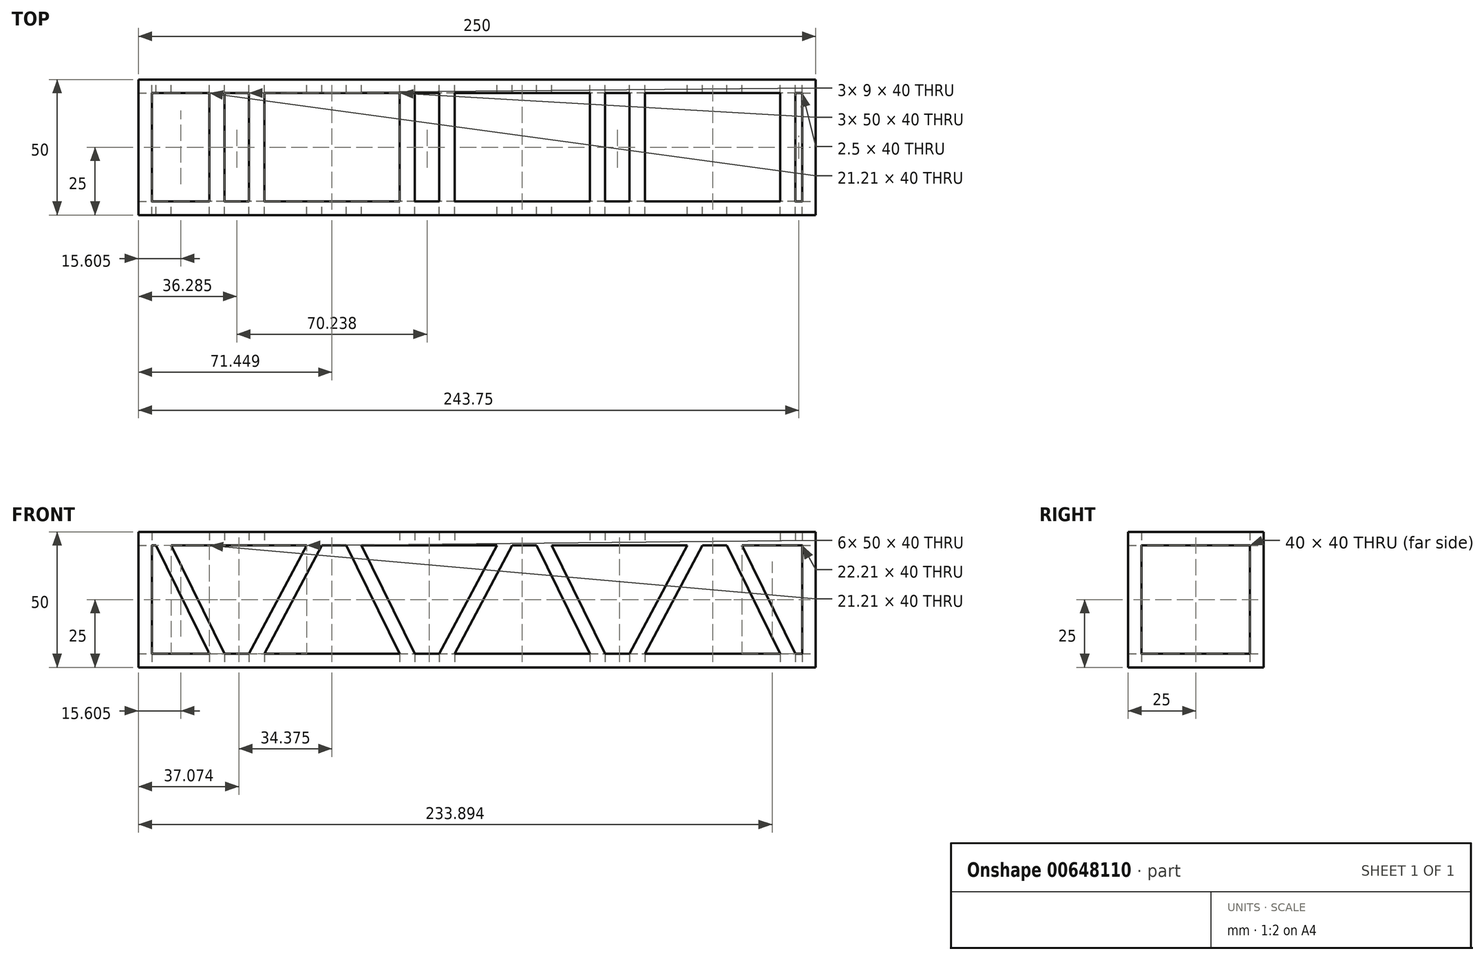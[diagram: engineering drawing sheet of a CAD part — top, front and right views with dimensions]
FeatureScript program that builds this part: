
annotation { "Feature Type Name" : "Feature", "Feature Type Description" : "" }
export const myFeature = defineFeature(function(context is Context, id is Id, definition is map)
    precondition{}
    {
        {
            var Q0;
            Q0=qCreatedBy(makeId("Front.planeOp"),FACE);
            var sketch = newSketch(context, id + "F0", { "sketchPlane" : qUnion([Q0])});
            skLineSegment(sketch, "E0", {"start": v(-152.14, 45) * mm, "end": v(97.86, 45) * mm});
            skLineSegment(sketch, "E1", {"start": v(97.86, 45) * mm, "end": v(97.86, -5) * mm});
            skLineSegment(sketch, "E2", {"start": v(97.86, -5) * mm, "end": v(-152.14, -5) * mm});
            skLineSegment(sketch, "E3", {"start": v(-152.14, -5) * mm, "end": v(-152.14, 45) * mm});
            skLineSegment(sketch, "E4", {"start": v(-145.64, 40) * mm, "end": v(-125.93, 0) * mm});
            skLineSegment(sketch, "E5", {"start": v(-111.35, 0) * mm, "end": v(-90.07, 40) * mm});
            skLineSegment(sketch, "E6", {"start": v(-69.83, 40) * mm, "end": v(-50.12, 0) * mm});
            skLineSegment(sketch, "E7", {"start": v(-41.12, 0) * mm, "end": v(-19.83, 40) * mm});
            skLineSegment(sketch, "E8", {"start": v(-5.16, 40) * mm, "end": v(14.55, 0) * mm});
            skLineSegment(sketch, "E9.0", {"start": v(84.79, 0) * mm, "end": v(34.79, 0) * mm});
            skLineSegment(sketch, "E10.0", {"start": v(-105.7, 0) * mm, "end": v(-84.4, 40) * mm});
            skLineSegment(sketch, "E11.0", {"start": v(0.41, 40) * mm, "end": v(20.12, 0) * mm});
            skLineSegment(sketch, "E12.0", {"start": v(34.79, 0) * mm, "end": v(56.07, 40) * mm});
            skLineSegment(sketch, "E13.trimOffspring", {"start": v(-140.07, 40) * mm, "end": v(-120.35, 0) * mm});
            skLineSegment(sketch, "E14.trimOffspring", {"start": v(-140.07, 40) * mm, "end": v(-90.07, 40) * mm});
            skLineSegment(sketch, "E15.trimOffspring", {"start": v(-75.4, 40) * mm, "end": v(-55.7, 0) * mm});
            skLineSegment(sketch, "E16.trimOffspring", {"start": v(-69.83, 40) * mm, "end": v(-19.83, 40) * mm});
            skLineSegment(sketch, "E17.trimOffspring", {"start": v(-84.4, 40) * mm, "end": v(-75.4, 40) * mm});
            skLineSegment(sketch, "E18.trimOffspring", {"start": v(-111.35, 0) * mm, "end": v(-120.35, 0) * mm});
            skLineSegment(sketch, "E19.trimOffspring", {"start": v(-125.93, 0) * mm, "end": v(-147.14, 0) * mm});
            skLineSegment(sketch, "E20.trimOffspring", {"start": v(-14.16, 40) * mm, "end": v(-5.16, 40) * mm});
            skLineSegment(sketch, "E21", {"start": v(0.41, 40) * mm, "end": v(50.41, 40) * mm});
            skLineSegment(sketch, "E22.trimOffspring", {"start": v(29.12, 0) * mm, "end": v(50.41, 40) * mm});
            skLineSegment(sketch, "E23.trimOffspring", {"start": v(-35.45, 0) * mm, "end": v(-14.16, 40) * mm});
            skLineSegment(sketch, "E24.trimOffspring", {"start": v(-55.7, 0) * mm, "end": v(-105.7, 0) * mm});
            skLineSegment(sketch, "E25.trimOffspring", {"start": v(-41.12, 0) * mm, "end": v(-50.12, 0) * mm});
            skLineSegment(sketch, "E26.trimOffspring", {"start": v(14.55, 0) * mm, "end": v(-35.45, 0) * mm});
            skLineSegment(sketch, "E27.trimOffspring", {"start": v(29.12, 0) * mm, "end": v(20.12, 0) * mm});
            skLineSegment(sketch, "E28", {"start": v(-147.14, 40) * mm, "end": v(-147.14, 0) * mm});
            skLineSegment(sketch, "E29", {"start": v(70.65, 40) * mm, "end": v(92.86, 40) * mm});
            skLineSegment(sketch, "E30", {"start": v(65.07, 40) * mm, "end": v(84.79, 0) * mm});
            skLineSegment(sketch, "E31", {"start": v(70.65, 40) * mm, "end": v(90.36, 0) * mm});
            skLineSegment(sketch, "E32", {"start": v(56.07, 40) * mm, "end": v(65.07, 40) * mm});
            skLineSegment(sketch, "E33", {"start": v(90.36, 0) * mm, "end": v(97.86, 0) * mm});
            skLineSegment(sketch, "E34", {"start": v(92.86, 0) * mm, "end": v(92.86, 40) * mm});
            skLineSegment(sketch, "E35", {"start": v(-147.14, 40) * mm, "end": v(-145.64, 40) * mm});
            skPoint(sketch, "E36.orphan", {"position": v(92.86, -5.07) * mm});
            skSolve(sketch);
        }
        {
            var Q0;
            {var subQ3=sQuery(id+"F0.wireOp",EDGE,"E0");Q0=makeQuery(id+"F0.imprint","IMPRINT",FACE,{"disambiguationData":[TD([[makeQuery(id+"F0.imprint","IMPRINT",EDGE,{"derivedFrom":subQ3}),-1.0]])]});}
            extrude(context, id + "F1", {"entities" : qUnion([Q0]), "depth" : 50 * mm, "offsetDistance" : 25 * mm});
        }
        {
            var Q0;
            Q0=makeQuery(id+"F1.opExtrude","SWEPT_FACE",FACE,{"disambiguationData":[OSD([sQuery(id+"F0.wireOp",EDGE,"E2")])]});
            var sketch = newSketch(context, id + "F2", { "sketchPlane" : qUnion([Q0])});
            skLineSegment(sketch, "E37.bottom", {"start": v(-147.14, 45) * mm, "end": v(-125.93, 45) * mm});
            skLineSegment(sketch, "E37.top", {"start": v(-147.14, 5) * mm, "end": v(-125.93, 5) * mm});
            skLineSegment(sketch, "E37.left", {"start": v(-147.14, 45) * mm, "end": v(-147.14, 5) * mm});
            skLineSegment(sketch, "E37.right", {"start": v(-125.93, 45) * mm, "end": v(-125.93, 5) * mm});
            skLineSegment(sketch, "E38.bottom", {"start": v(-120.35, 45) * mm, "end": v(-111.35, 45) * mm});
            skLineSegment(sketch, "E38.top", {"start": v(-120.35, 5) * mm, "end": v(-111.35, 5) * mm});
            skLineSegment(sketch, "E38.left", {"start": v(-120.35, 45) * mm, "end": v(-120.35, 5) * mm});
            skLineSegment(sketch, "E38.right", {"start": v(-111.35, 45) * mm, "end": v(-111.35, 5) * mm});
            skLineSegment(sketch, "E39.bottom", {"start": v(-105.7, 45) * mm, "end": v(-55.7, 45) * mm});
            skLineSegment(sketch, "E39.top", {"start": v(-105.7, 5) * mm, "end": v(-55.7, 5) * mm});
            skLineSegment(sketch, "E39.left", {"start": v(-105.7, 45) * mm, "end": v(-105.7, 5) * mm});
            skLineSegment(sketch, "E39.right", {"start": v(-55.7, 45) * mm, "end": v(-55.7, 5) * mm});
            skLineSegment(sketch, "E40.bottom", {"start": v(-50.12, 45) * mm, "end": v(-41.12, 45) * mm});
            skLineSegment(sketch, "E40.top", {"start": v(-50.12, 5) * mm, "end": v(-41.12, 5) * mm});
            skLineSegment(sketch, "E40.left", {"start": v(-50.12, 45) * mm, "end": v(-50.12, 5) * mm});
            skLineSegment(sketch, "E40.right", {"start": v(-41.12, 45) * mm, "end": v(-41.12, 5) * mm});
            skLineSegment(sketch, "E41.bottom", {"start": v(-35.45, 45) * mm, "end": v(14.55, 45) * mm});
            skLineSegment(sketch, "E41.top", {"start": v(-35.45, 5) * mm, "end": v(14.55, 5) * mm});
            skLineSegment(sketch, "E41.left", {"start": v(-35.45, 45) * mm, "end": v(-35.45, 5) * mm});
            skLineSegment(sketch, "E41.right", {"start": v(14.55, 45) * mm, "end": v(14.55, 5) * mm});
            skLineSegment(sketch, "E42.bottom", {"start": v(20.12, 45) * mm, "end": v(29.12, 45) * mm});
            skLineSegment(sketch, "E42.top", {"start": v(20.12, 5) * mm, "end": v(29.12, 5) * mm});
            skLineSegment(sketch, "E42.left", {"start": v(20.12, 45) * mm, "end": v(20.12, 5) * mm});
            skLineSegment(sketch, "E42.right", {"start": v(29.12, 45) * mm, "end": v(29.12, 5) * mm});
            skLineSegment(sketch, "E43.bottom", {"start": v(34.79, 45) * mm, "end": v(84.79, 45) * mm});
            skLineSegment(sketch, "E43.top", {"start": v(34.79, 5) * mm, "end": v(84.79, 5) * mm});
            skLineSegment(sketch, "E43.left", {"start": v(34.79, 45) * mm, "end": v(34.79, 5) * mm});
            skLineSegment(sketch, "E43.right", {"start": v(84.79, 45) * mm, "end": v(84.79, 5) * mm});
            skLineSegment(sketch, "E44.bottom", {"start": v(90.36, 45) * mm, "end": v(92.86, 45) * mm});
            skLineSegment(sketch, "E44.top", {"start": v(90.36, 5) * mm, "end": v(92.86, 5) * mm});
            skLineSegment(sketch, "E44.left", {"start": v(90.36, 45) * mm, "end": v(90.36, 5) * mm});
            skLineSegment(sketch, "E44.right", {"start": v(92.86, 45) * mm, "end": v(92.86, 5) * mm});
            skSolve(sketch);
        }
        {
            var Q0;
            Q0=makeQuery(id+"F2.imprint","IMPRINT",FACE,{"disambiguationData":[TD([[makeQuery(id+"F2.imprint","IMPRINT",EDGE,{"derivedFrom":sQuery(id+"F2.wireOp",EDGE,"E44.bottom")}),-1.0]])]});
            var Q1;
            Q1=makeQuery(id+"F2.imprint","IMPRINT",FACE,{"disambiguationData":[TD([[makeQuery(id+"F2.imprint","IMPRINT",EDGE,{"derivedFrom":sQuery(id+"F2.wireOp",EDGE,"E43.bottom")}),-1.0]])]});
            var Q2;
            Q2=makeQuery(id+"F2.imprint","IMPRINT",FACE,{"disambiguationData":[TD([[makeQuery(id+"F2.imprint","IMPRINT",EDGE,{"derivedFrom":sQuery(id+"F2.wireOp",EDGE,"E41.bottom")}),-1.0]])]});
            var Q3;
            Q3=makeQuery(id+"F2.imprint","IMPRINT",FACE,{"disambiguationData":[TD([[makeQuery(id+"F2.imprint","IMPRINT",EDGE,{"derivedFrom":sQuery(id+"F2.wireOp",EDGE,"E42.bottom")}),-1.0]])]});
            var Q4;
            Q4=makeQuery(id+"F2.imprint","IMPRINT",FACE,{"disambiguationData":[TD([[makeQuery(id+"F2.imprint","IMPRINT",EDGE,{"derivedFrom":sQuery(id+"F2.wireOp",EDGE,"E39.bottom")}),-1.0]])]});
            var Q5;
            Q5=makeQuery(id+"F2.imprint","IMPRINT",FACE,{"disambiguationData":[TD([[makeQuery(id+"F2.imprint","IMPRINT",EDGE,{"derivedFrom":sQuery(id+"F2.wireOp",EDGE,"E40.bottom")}),-1.0]])]});
            var Q6;
            Q6=makeQuery(id+"F2.imprint","IMPRINT",FACE,{"disambiguationData":[TD([[makeQuery(id+"F2.imprint","IMPRINT",EDGE,{"derivedFrom":sQuery(id+"F2.wireOp",EDGE,"E37.bottom")}),-1.0]])]});
            var Q7;
            Q7=makeQuery(id+"F2.imprint","IMPRINT",FACE,{"disambiguationData":[TD([[makeQuery(id+"F2.imprint","IMPRINT",EDGE,{"derivedFrom":sQuery(id+"F2.wireOp",EDGE,"E38.bottom")}),-1.0]])]});
            extrude(context, id + "F3", {"entities" : qUnion([Q0, Q1, Q2, Q3, Q4, Q5, Q6, Q7]), "operationType" : NewBodyOperationType.REMOVE, "oppositeDirection" : true, "depth" : 5 * mm, "offsetDistance" : 25 * mm});
        }
        {
            var Q0;
            Q0=makeQuery(id+"F1.opExtrude","SWEPT_FACE",FACE,{"disambiguationData":[OSD([sQuery(id+"F0.wireOp",EDGE,"E1")])]});
            var sketch = newSketch(context, id + "F4", { "sketchPlane" : qUnion([Q0])});
            skLineSegment(sketch, "E45.bottom", {"start": v(-5, 0) * mm, "end": v(-45, 0) * mm});
            skLineSegment(sketch, "E45.top", {"start": v(-5, 40) * mm, "end": v(-45, 40) * mm});
            skLineSegment(sketch, "E45.left", {"start": v(-5, 0) * mm, "end": v(-5, 40) * mm});
            skLineSegment(sketch, "E45.right", {"start": v(-45, 0) * mm, "end": v(-45, 40) * mm});
            skSolve(sketch);
        }
        {
            var Q0;
            Q0=makeQuery(id+"F4.imprint","IMPRINT",FACE,{"disambiguationData":[TD([[makeQuery(id+"F4.imprint","IMPRINT",EDGE,{"derivedFrom":sQuery(id+"F4.wireOp",EDGE,"E45.bottom")}),-1.0]])]});
            extrude(context, id + "F5", {"entities" : qUnion([Q0]), "operationType" : NewBodyOperationType.REMOVE, "oppositeDirection" : true, "depth" : 350 * mm, "offsetDistance" : 25 * mm});
        }
        {
            var Q0;
            Q0=makeQuery(id+"F5.boolean.opBoolean","MERGE",FACE,{"derivedFrom":[makeQuery(id+"F1.opExtrude","SWEPT_FACE",FACE,{"disambiguationData":[OSD([sQuery(id+"F0.wireOp",EDGE,"E14.trimOffspring")])]}),makeQuery(id+"F1.opExtrude","SWEPT_FACE",FACE,{"disambiguationData":[OSD([sQuery(id+"F0.wireOp",EDGE,"E16.trimOffspring")])]}),makeQuery(id+"F1.opExtrude","SWEPT_FACE",FACE,{"disambiguationData":[OSD([sQuery(id+"F0.wireOp",EDGE,"E17.trimOffspring")])]}),makeQuery(id+"F1.opExtrude","SWEPT_FACE",FACE,{"disambiguationData":[OSD([sQuery(id+"F0.wireOp",EDGE,"E20.trimOffspring")])]}),makeQuery(id+"F1.opExtrude","SWEPT_FACE",FACE,{"disambiguationData":[OSD([sQuery(id+"F0.wireOp",EDGE,"E21")])]}),makeQuery(id+"F1.opExtrude","SWEPT_FACE",FACE,{"disambiguationData":[OSD([sQuery(id+"F0.wireOp",EDGE,"E29")])]}),makeQuery(id+"F1.opExtrude","SWEPT_FACE",FACE,{"disambiguationData":[OSD([sQuery(id+"F0.wireOp",EDGE,"E32")])]}),makeQuery(id+"F1.opExtrude","SWEPT_FACE",FACE,{"disambiguationData":[OSD([sQuery(id+"F0.wireOp",EDGE,"E35")])]}),makeQuery(id+"F5.opExtrude","SWEPT_FACE",FACE,{"disambiguationData":[OSD([sQuery(id+"F4.wireOp",EDGE,"E45.top")])]})]});
            var sketch = newSketch(context, id + "F6", { "sketchPlane" : qUnion([Q0])});
            skLineSegment(sketch, "E46.bottom", {"start": v(92.86, 5) * mm, "end": v(90.36, 5) * mm});
            skLineSegment(sketch, "E46.top", {"start": v(92.86, 45) * mm, "end": v(90.36, 45) * mm});
            skLineSegment(sketch, "E46.left", {"start": v(92.86, 5) * mm, "end": v(92.86, 45) * mm});
            skLineSegment(sketch, "E46.right", {"start": v(90.36, 5) * mm, "end": v(90.36, 45) * mm});
            skLineSegment(sketch, "E47.bottom", {"start": v(84.79, 45) * mm, "end": v(34.79, 45) * mm});
            skLineSegment(sketch, "E47.top", {"start": v(84.79, 5) * mm, "end": v(34.79, 5) * mm});
            skLineSegment(sketch, "E47.left", {"start": v(84.79, 45) * mm, "end": v(84.79, 5) * mm});
            skLineSegment(sketch, "E47.right", {"start": v(34.79, 45) * mm, "end": v(34.79, 5) * mm});
            skLineSegment(sketch, "E48.bottom", {"start": v(20.12, 5) * mm, "end": v(29.12, 5) * mm});
            skLineSegment(sketch, "E48.top", {"start": v(20.12, 45) * mm, "end": v(29.12, 45) * mm});
            skLineSegment(sketch, "E48.left", {"start": v(20.12, 5) * mm, "end": v(20.12, 45) * mm});
            skLineSegment(sketch, "E48.right", {"start": v(29.12, 5) * mm, "end": v(29.12, 45) * mm});
            skLineSegment(sketch, "E49.bottom", {"start": v(14.55, 5) * mm, "end": v(-35.45, 5) * mm});
            skLineSegment(sketch, "E49.top", {"start": v(14.55, 45) * mm, "end": v(-35.45, 45) * mm});
            skLineSegment(sketch, "E49.right", {"start": v(-35.45, 5) * mm, "end": v(-35.45, 45) * mm});
            skLineSegment(sketch, "E50.bottom", {"start": v(-41.12, 45) * mm, "end": v(-50.12, 45) * mm});
            skLineSegment(sketch, "E50.top", {"start": v(-41.12, 5) * mm, "end": v(-50.12, 5) * mm});
            skLineSegment(sketch, "E50.left", {"start": v(-41.12, 45) * mm, "end": v(-41.12, 5) * mm});
            skLineSegment(sketch, "E50.right", {"start": v(-50.12, 45) * mm, "end": v(-50.12, 5) * mm});
            skLineSegment(sketch, "E51.bottom", {"start": v(-111.35, 5) * mm, "end": v(-120.35, 5) * mm});
            skLineSegment(sketch, "E51.top", {"start": v(-111.35, 45) * mm, "end": v(-120.35, 45) * mm});
            skLineSegment(sketch, "E51.left", {"start": v(-111.35, 5) * mm, "end": v(-111.35, 45) * mm});
            skLineSegment(sketch, "E51.right", {"start": v(-120.35, 5) * mm, "end": v(-120.35, 45) * mm});
            skLineSegment(sketch, "E52.bottom", {"start": v(-125.93, 5) * mm, "end": v(-147.14, 5) * mm});
            skLineSegment(sketch, "E52.top", {"start": v(-125.93, 45) * mm, "end": v(-147.14, 45) * mm});
            skLineSegment(sketch, "E52.left", {"start": v(-125.93, 5) * mm, "end": v(-125.93, 45) * mm});
            skLineSegment(sketch, "E52.right", {"start": v(-147.14, 5) * mm, "end": v(-147.14, 45) * mm});
            skLineSegment(sketch, "E53", {"start": v(14.55, 45) * mm, "end": v(14.55, 5) * mm});
            skLineSegment(sketch, "E54.bottom", {"start": v(-55.7, 45) * mm, "end": v(-105.7, 45) * mm});
            skLineSegment(sketch, "E54.top", {"start": v(-55.7, 5) * mm, "end": v(-105.7, 5) * mm});
            skLineSegment(sketch, "E54.left", {"start": v(-55.7, 45) * mm, "end": v(-55.7, 5) * mm});
            skLineSegment(sketch, "E54.right", {"start": v(-105.7, 45) * mm, "end": v(-105.7, 5) * mm});
            skSolve(sketch);
        }
        {
            var Q0;
            {var subQ53=sQuery(id+"F6.wireOp",EDGE,"E52.left");Q0=makeQuery(id+"F6.imprint","IMPRINT",FACE,{"disambiguationData":[TD([[makeQuery(id+"F6.imprint","IMPRINT",EDGE,{"derivedFrom":subQ53}),1.0]])]});}
            var Q1;
            Q1=makeQuery(id+"F6.imprint","IMPRINT",FACE,{"disambiguationData":[TD([[makeQuery(id+"F6.imprint","IMPRINT",EDGE,{"derivedFrom":sQuery(id+"F6.wireOp",EDGE,"E51.bottom")}),-1.0]])]});
            var Q2;
            {var subQ60=sQuery(id+"F6.wireOp",EDGE,"E49.right");Q2=makeQuery(id+"F6.imprint","IMPRINT",FACE,{"disambiguationData":[TD([[makeQuery(id+"F6.imprint","IMPRINT",EDGE,{"derivedFrom":subQ60}),-1.0]])]});}
            var Q3;
            {var subQ61=sQuery(id+"F6.wireOp",EDGE,"E54.left");Q3=makeQuery(id+"F6.imprint","IMPRINT",FACE,{"disambiguationData":[TD([[makeQuery(id+"F6.imprint","IMPRINT",EDGE,{"derivedFrom":subQ61}),-1.0]])]});}
            var Q4;
            Q4=makeQuery(id+"F6.imprint","IMPRINT",FACE,{"disambiguationData":[TD([[makeQuery(id+"F6.imprint","IMPRINT",EDGE,{"derivedFrom":sQuery(id+"F6.wireOp",EDGE,"E50.bottom")}),1.0]])]});
            var Q5;
            Q5=makeQuery(id+"F6.imprint","IMPRINT",FACE,{"disambiguationData":[TD([[makeQuery(id+"F6.imprint","IMPRINT",EDGE,{"derivedFrom":sQuery(id+"F6.wireOp",EDGE,"E48.bottom")}),1.0]])]});
            var Q6;
            {var subQ61=sQuery(id+"F6.wireOp",EDGE,"E47.left");Q6=makeQuery(id+"F6.imprint","IMPRINT",FACE,{"disambiguationData":[TD([[makeQuery(id+"F6.imprint","IMPRINT",EDGE,{"derivedFrom":subQ61}),-1.0]])]});}
            var Q7;
            Q7=makeQuery(id+"F6.imprint","IMPRINT",FACE,{"disambiguationData":[TD([[makeQuery(id+"F6.imprint","IMPRINT",EDGE,{"derivedFrom":sQuery(id+"F6.wireOp",EDGE,"E46.bottom")}),-1.0]])]});
            extrude(context, id + "F7", {"entities" : qUnion([Q0, Q1, Q2, Q3, Q4, Q5, Q6, Q7]), "operationType" : NewBodyOperationType.REMOVE, "oppositeDirection" : true, "depth" : 25 * mm, "offsetDistance" : 25 * mm});
        }
    });
